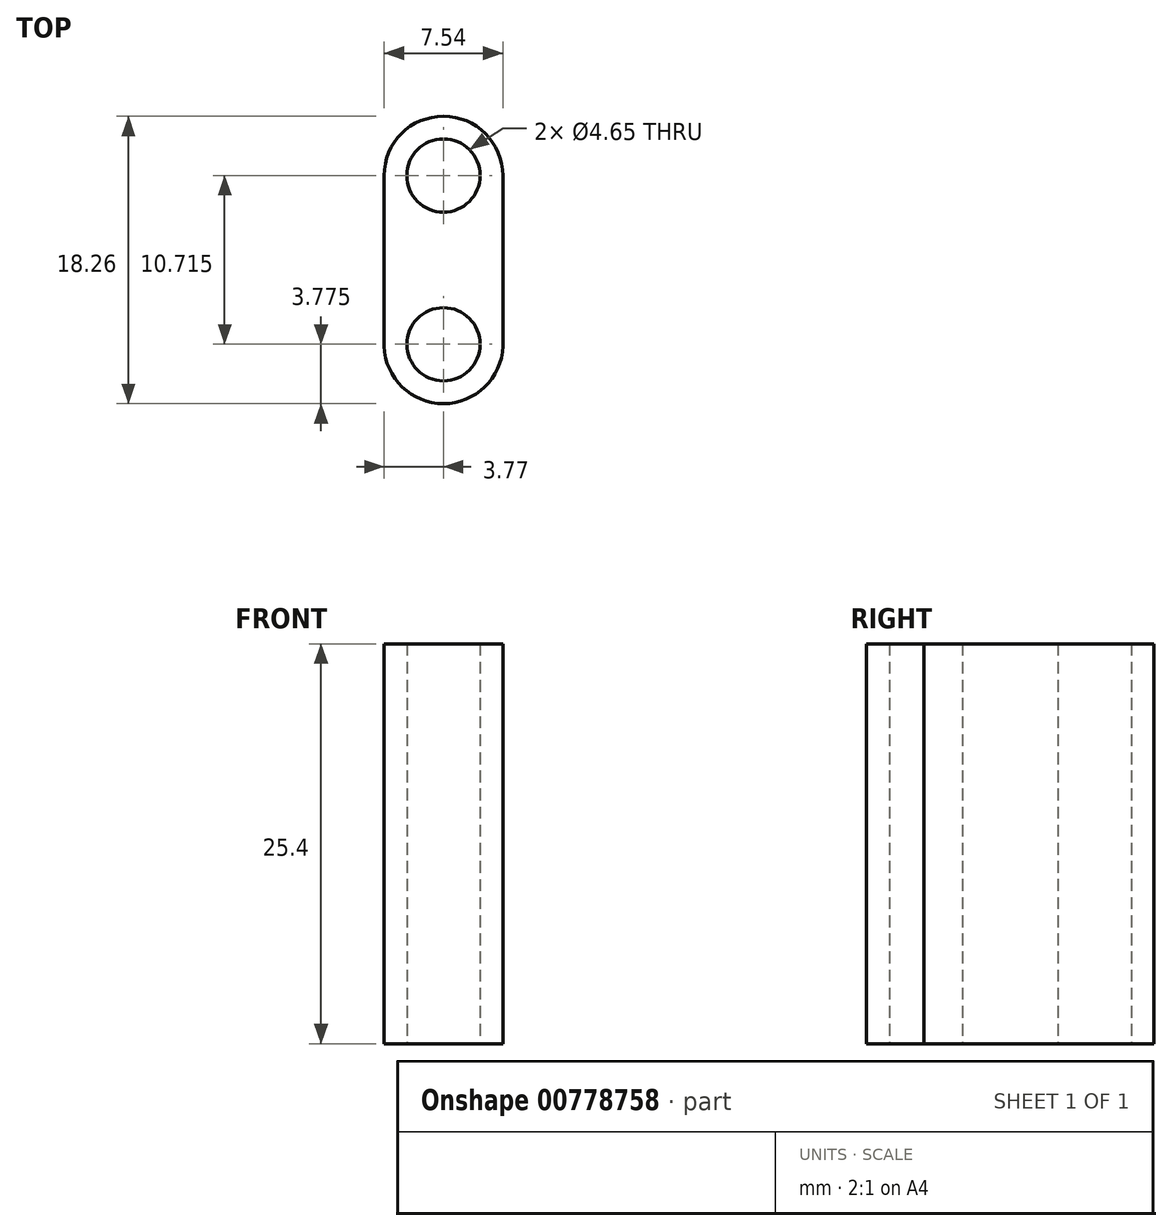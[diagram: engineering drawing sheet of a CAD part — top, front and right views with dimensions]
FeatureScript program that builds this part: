
annotation { "Feature Type Name" : "Feature", "Feature Type Description" : "" }
export const myFeature = defineFeature(function(context is Context, id is Id, definition is map)
    precondition{}
    {
        {
            var Q0;
            Q0=qCreatedBy(makeId("Top.planeOp"),FACE);
            var sketch = newSketch(context, id + "F0", { "sketchPlane" : qUnion([Q0])});
            skCircle(sketch, "E0", {"center": v(0, 0) * mm, "radius": 2.33 * mm});
            skCircle(sketch, "E1", {"center": v(0, 0) * mm, "radius": 3.77 * mm});
            skCircle(sketch, "E2", {"center": v(0, -10.72) * mm, "radius": 3.77 * mm});
            skCircle(sketch, "E3", {"center": v(0, -10.72) * mm, "radius": 2.32 * mm});
            skLineSegment(sketch, "E4", {"start": v(-3.77, 0) * mm, "end": v(-3.77, -10.84) * mm});
            skLineSegment(sketch, "E5", {"start": v(3.77, 0) * mm, "end": v(3.77, -10.84) * mm});
            skSolve(sketch);
        }
        {
            var Q0;
            Q0=makeQuery(id+"F0.imprint","IMPRINT",FACE,{"disambiguationData":[TD([[makeQuery(id+"F0.imprint","IMPRINT",EDGE,{"derivedFrom":sQuery(id+"F0.wireOp",EDGE,"E0")}),-1.0]])]});
            var Q1;
            Q1=makeQuery(id+"F0.imprint","IMPRINT",FACE,{"disambiguationData":[TD([[makeQuery(id+"F0.imprint","IMPRINT",EDGE,{"derivedFrom":sQuery(id+"F0.wireOp",EDGE,"E3")}),-1.0]])]});
            var Q2;
            {var subQ0=sQuery(id+"F0.wireOp",EDGE,"E4");var subQ1=sQuery(id+"F0.wireOp",EDGE,"E1");var subQ2=makeQuery(id+"F0.imprint","INTERSECT",VERTEX,{"derivedFrom":[subQ1,subQ0]});Q2=makeQuery(id+"F0.imprint","IMPRINT",FACE,{"disambiguationData":[TD([[makeQuery(id+"F0.imprint","IMPRINT",EDGE,{"disambiguationData":[TD([[subQ2,-1.0]])],"derivedFrom":subQ1}),-1.0]])]});}
            extrude(context, id + "F1", {"entities" : qUnion([Q0, Q1, Q2]), "depth" : 25.4 * mm, "offsetDistance" : 25.4 * mm});
        }
    });
